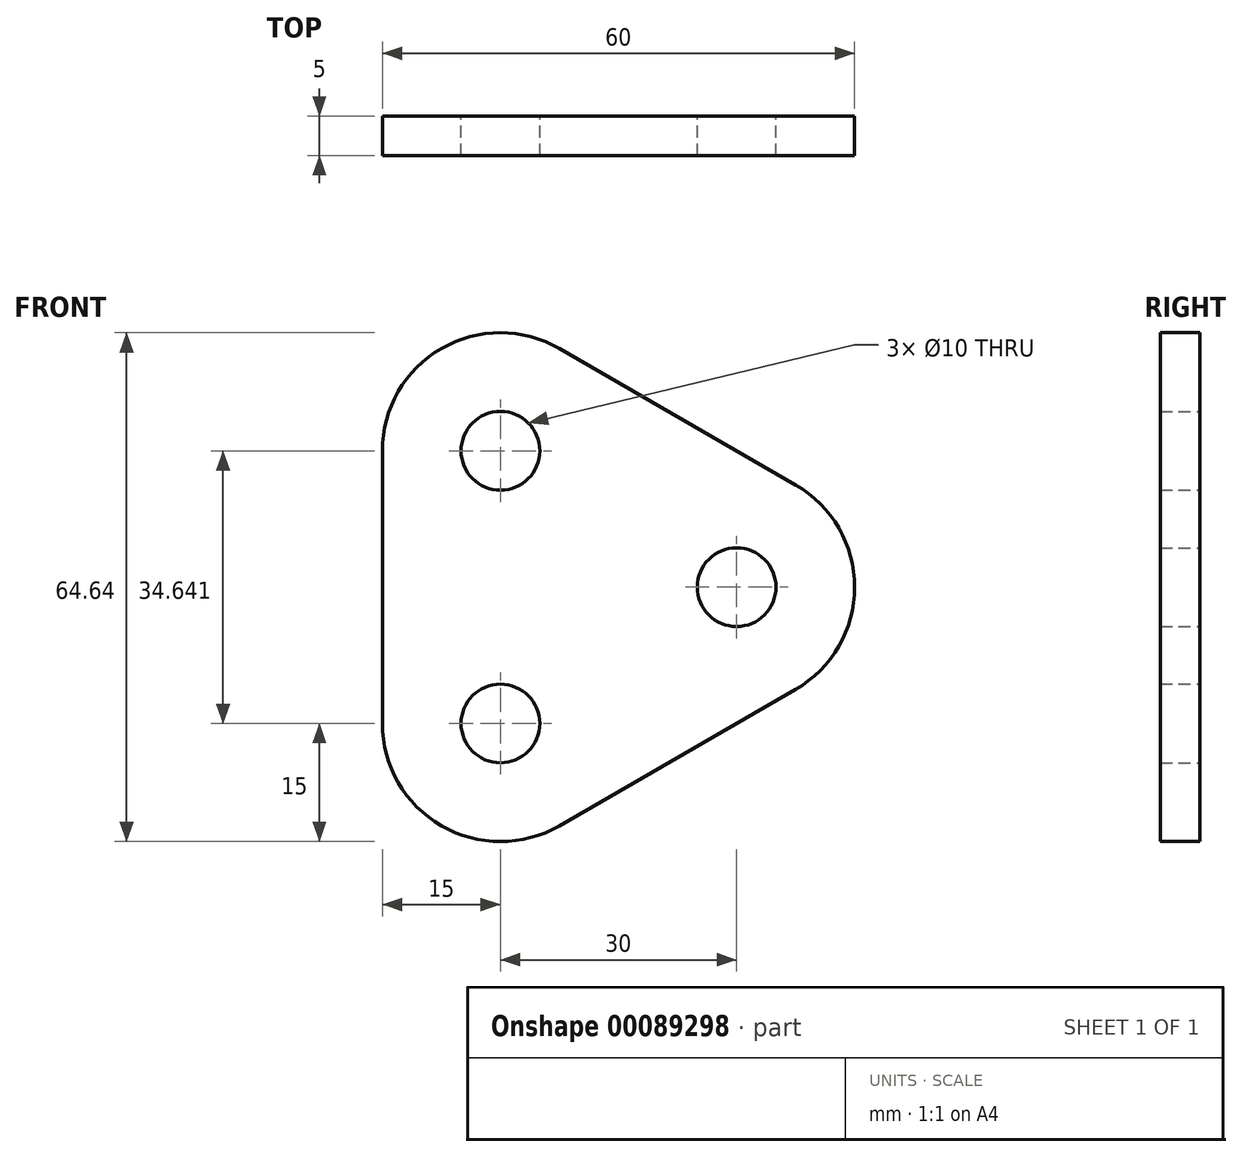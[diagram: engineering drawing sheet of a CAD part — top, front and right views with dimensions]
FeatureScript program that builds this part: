
annotation { "Feature Type Name" : "Feature", "Feature Type Description" : "" }
export const myFeature = defineFeature(function(context is Context, id is Id, definition is map)
    precondition{}
    {
        {
            var Q0;
            Q0=qCreatedBy(makeId("Front.planeOp"),FACE);
            var sketch = newSketch(context, id + "F0", { "sketchPlane" : qUnion([Q0])});
            skCircle(sketch, "E0", {"center": v(0, 0) * mm, "radius": 20 * mm, "construction": true});
            skLineSegment(sketch, "E1.0", {"start": v(-25, -17.32) * mm, "end": v(-25, 17.32) * mm});
            skLineSegment(sketch, "E1.1", {"start": v(-2.5, 30.31) * mm, "end": v(27.5, 13) * mm});
            skLineSegment(sketch, "E1.2", {"start": v(27.5, -13) * mm, "end": v(-2.5, -30.31) * mm});
            skPoint(sketch, "E1.0.midPoint", {"position": v(-25, 0) * mm});
            skPoint(sketch, "E2.visualSharp", {"position": v(-25, 43.3) * mm});
            skArc(sketch, "E2.filletArc", {"start": v(-2.5, 30.31) * mm, "mid": v(-17.5, 30.31) * mm, "end": v(-25, 17.32) * mm});
            skPoint(sketch, "E3.visualSharp", {"position": v(-25, -43.3) * mm});
            skArc(sketch, "E3.filletArc", {"start": v(-25, -17.32) * mm, "mid": v(-17.5, -30.31) * mm, "end": v(-2.5, -30.31) * mm});
            skPoint(sketch, "E4.visualSharp", {"position": v(50, 0) * mm});
            skArc(sketch, "E4.filletArc", {"start": v(27.5, -13) * mm, "mid": v(35, 0) * mm, "end": v(27.5, 13) * mm});
            skCircle(sketch, "E5", {"center": v(-10, 17.32) * mm, "radius": 5 * mm});
            skCircle(sketch, "E6", {"center": v(-10, -17.32) * mm, "radius": 5 * mm});
            skCircle(sketch, "E7", {"center": v(20, 0) * mm, "radius": 5 * mm});
            skSolve(sketch);
        }
        {
            var Q0;
            Q0 = qSketchRegion(id + "F0", true);
            extrude(context, id + "F1", {"entities" : qUnion([Q0]), "depth" : 5 * mm});
        }
    });
